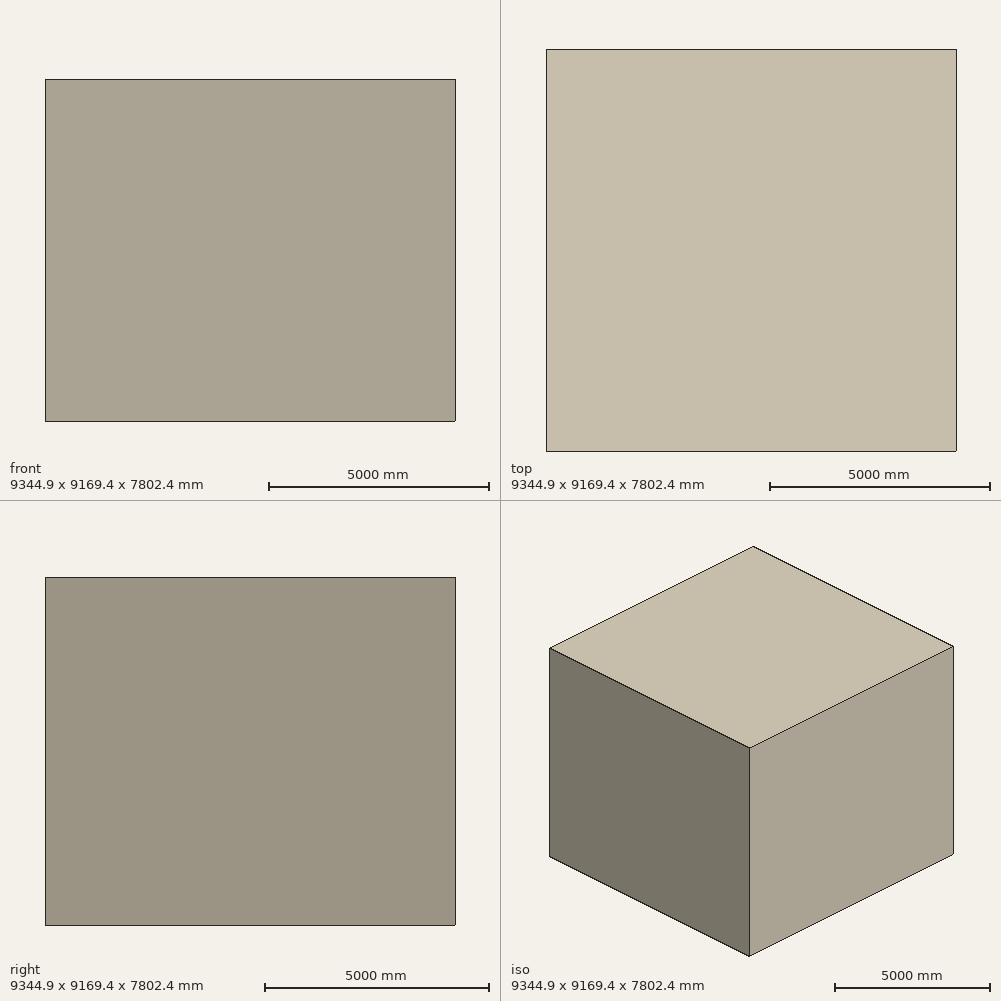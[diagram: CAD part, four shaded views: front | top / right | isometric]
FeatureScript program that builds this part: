
annotation { "Feature Type Name" : "Feature", "Feature Type Description" : "" }
export const myFeature = defineFeature(function(context is Context, id is Id, definition is map)
    precondition{}
    {
        {
            var Q0;
            Q0=qCreatedBy(makeId("Front.planeOp"),FACE);
            var sketch = newSketch(context, id + "F0", { "sketchPlane" : qUnion([Q0])});
            skLineSegment(sketch, "E0.bottom", {"start": v(762.6, -1666.83) * mm, "end": v(-8582.31, -1666.83) * mm});
            skLineSegment(sketch, "E0.top", {"start": v(762.6, 6135.59) * mm, "end": v(-8582.31, 6135.59) * mm});
            skLineSegment(sketch, "E0.left", {"start": v(762.6, -1666.83) * mm, "end": v(762.6, 6135.59) * mm});
            skLineSegment(sketch, "E0.right", {"start": v(-8582.31, -1666.83) * mm, "end": v(-8582.31, 6135.59) * mm});
            skSolve(sketch);
        }
        {
            var Q0;
            Q0=makeQuery(id+"F0.imprint","IMPRINT",FACE,{"disambiguationData":[TD([[makeQuery(id+"F0.imprint","IMPRINT",EDGE,{"derivedFrom":sQuery(id+"F0.wireOp",EDGE,"E0.bottom")}),-1.0]])]});
            extrude(context, id + "F1", {"entities" : qUnion([Q0]), "depth" : 9169.4 * mm});
        }
    });
